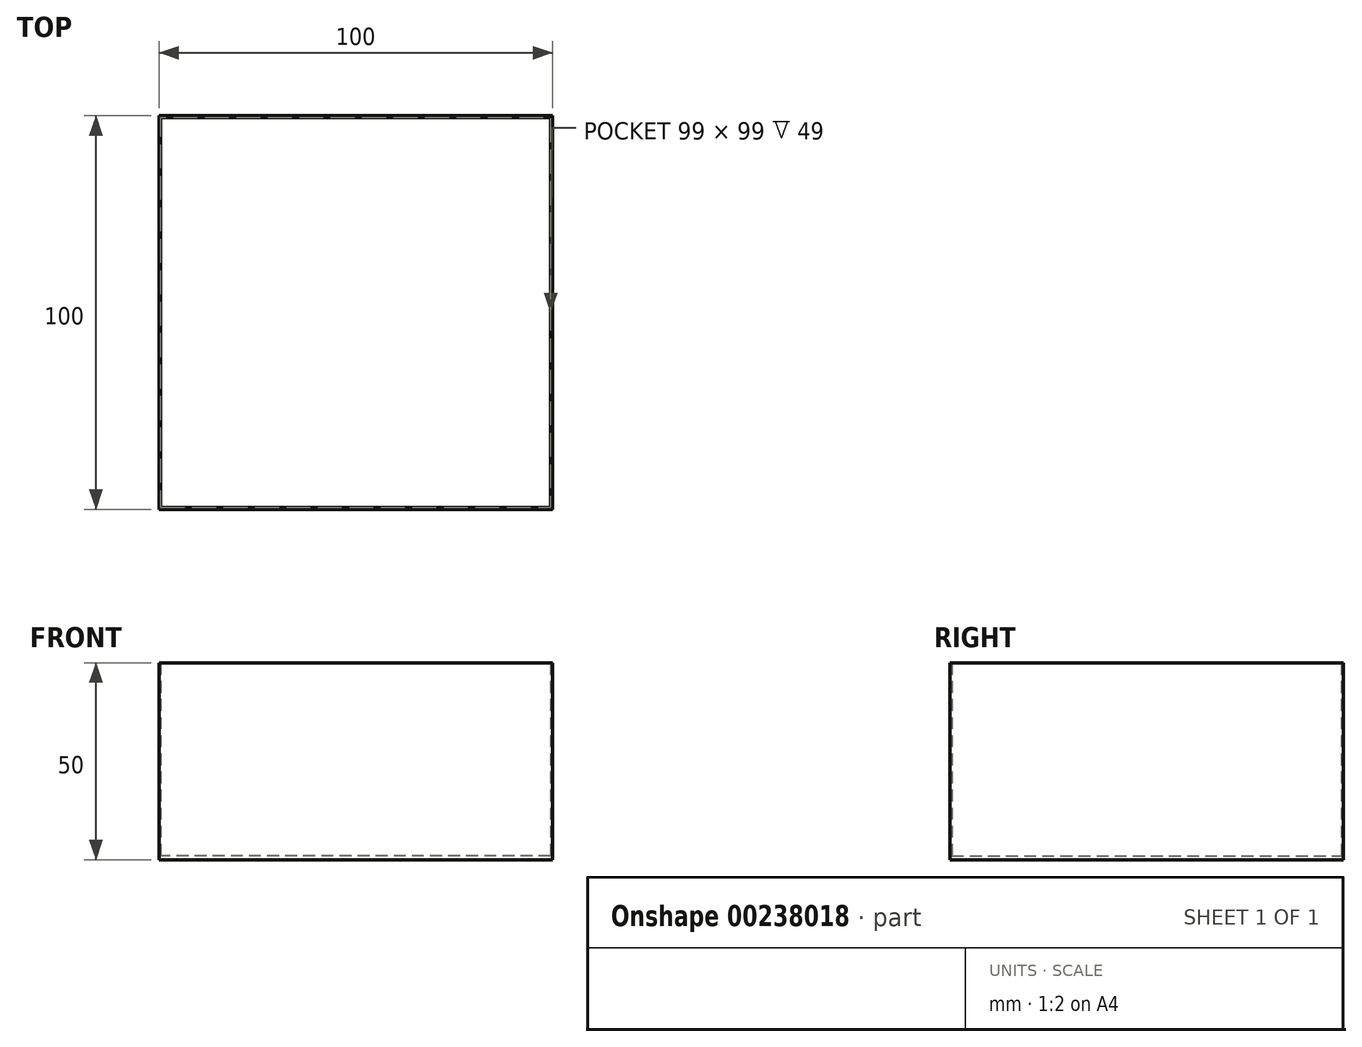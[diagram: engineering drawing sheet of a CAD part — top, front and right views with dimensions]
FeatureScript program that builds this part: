
annotation { "Feature Type Name" : "Feature", "Feature Type Description" : "" }
export const myFeature = defineFeature(function(context is Context, id is Id, definition is map)
    precondition{}
    {
        {
            var Q0;
            Q0=qCreatedBy(makeId("Front.planeOp"),FACE);
            var sketch = newSketch(context, id + "F0", { "sketchPlane" : qUnion([Q0])});
            skLineSegment(sketch, "E0", {"start": v(-50, 0) * mm, "end": v(-50, 50) * mm});
            skLineSegment(sketch, "E1", {"start": v(-50, 50) * mm, "end": v(-49.5, 50) * mm});
            skLineSegment(sketch, "E2", {"start": v(-49.5, 50) * mm, "end": v(-49.5, 1) * mm});
            skLineSegment(sketch, "E3", {"start": v(-49.5, 1) * mm, "end": v(0, 1) * mm});
            skLineSegment(sketch, "E4", {"start": v(0, 1) * mm, "end": v(0, 0) * mm});
            skLineSegment(sketch, "E5", {"start": v(0, 0) * mm, "end": v(-50, 0) * mm});
            skLineSegment(sketch, "E6.MirrorCS", {"start": v(49.5, 50) * mm, "end": v(49.5, 1) * mm});
            skLineSegment(sketch, "E7.MirrorCS", {"start": v(0, 0) * mm, "end": v(50, 0) * mm});
            skLineSegment(sketch, "E8.MirrorCS", {"start": v(49.5, 1) * mm, "end": v(0, 1) * mm});
            skLineSegment(sketch, "E9.MirrorCS", {"start": v(50, 0) * mm, "end": v(50, 50) * mm});
            skLineSegment(sketch, "E10.MirrorCS", {"start": v(50, 50) * mm, "end": v(49.5, 50) * mm});
            skSolve(sketch);
        }
        {
            var Q0;
            Q0=qCreatedBy(makeId("Right.planeOp"),FACE);
            var sketch = newSketch(context, id + "F1", { "sketchPlane" : qUnion([Q0])});
            skLineSegment(sketch, "E11", {"start": v(50, 50) * mm, "end": v(50, 0) * mm});
            skLineSegment(sketch, "E12", {"start": v(50, 0) * mm, "end": v(0, 0) * mm});
            skLineSegment(sketch, "E13", {"start": v(0, 0) * mm, "end": v(0, 1) * mm});
            skLineSegment(sketch, "E14", {"start": v(0, 1) * mm, "end": v(49.5, 1) * mm});
            skLineSegment(sketch, "E15", {"start": v(49.5, 1) * mm, "end": v(49.5, 50) * mm});
            skLineSegment(sketch, "E16", {"start": v(49.5, 50) * mm, "end": v(50, 50) * mm});
            skLineSegment(sketch, "E17.MirrorCS", {"start": v(-49.5, 50) * mm, "end": v(-50, 50) * mm});
            skLineSegment(sketch, "E18.MirrorCS", {"start": v(0, 1) * mm, "end": v(-49.5, 1) * mm});
            skLineSegment(sketch, "E19.MirrorCS", {"start": v(-50, 50) * mm, "end": v(-50, 0) * mm});
            skLineSegment(sketch, "E20.MirrorCS", {"start": v(-49.5, 1) * mm, "end": v(-49.5, 50) * mm});
            skLineSegment(sketch, "E21.MirrorCS", {"start": v(-50, 0) * mm, "end": v(0, 0) * mm});
            skSolve(sketch);
        }
        {
            var Q0;
            Q0 = qSketchRegion(id + "F0", true);
            extrude(context, id + "F2", {"entities" : qUnion([Q0]), "endBound" : BoundingType.SYMMETRIC, "depth" : 100 * mm});
        }
        {
            var Q0;
            Q0 = qSketchRegion(id + "F1", true);
            extrude(context, id + "F3", {"entities" : qUnion([Q0]), "operationType" : NewBodyOperationType.ADD, "endBound" : BoundingType.SYMMETRIC, "depth" : 100 * mm});
        }
    });
